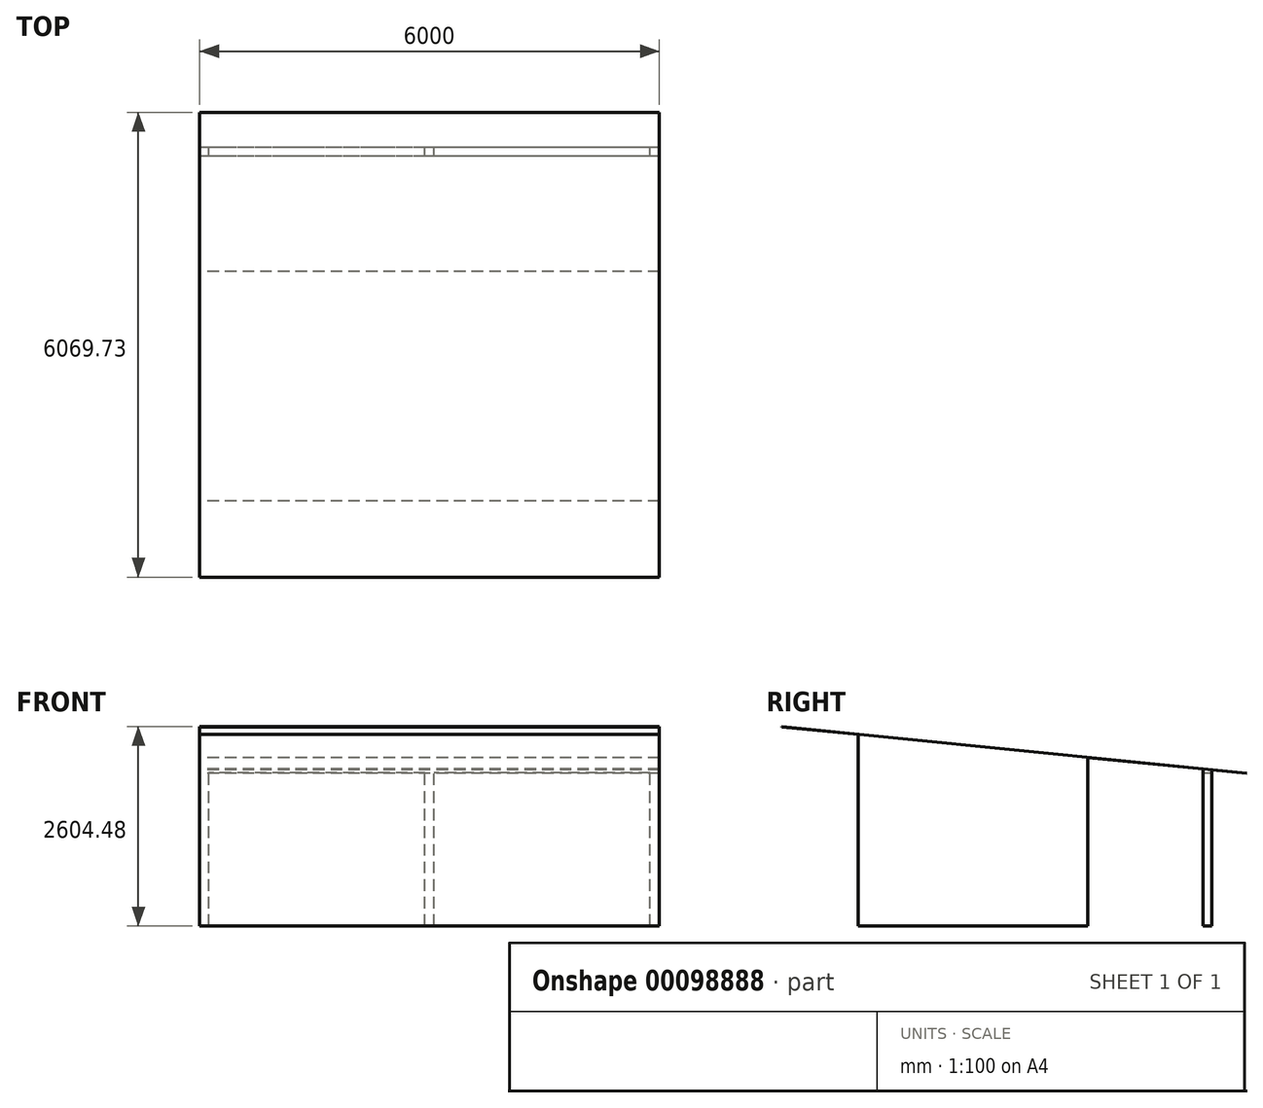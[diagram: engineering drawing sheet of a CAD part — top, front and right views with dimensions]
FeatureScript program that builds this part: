
annotation { "Feature Type Name" : "Feature", "Feature Type Description" : "" }
export const myFeature = defineFeature(function(context is Context, id is Id, definition is map)
    precondition{}
    {
        {
            var Q0;
            Q0=qCreatedBy(makeId("Right.planeOp"),FACE);
            var sketch = newSketch(context, id + "F0", { "sketchPlane" : qUnion([Q0])});
            skLineSegment(sketch, "E0", {"start": v(0, 0) * mm, "end": v(0, 2500) * mm});
            skLineSegment(sketch, "E1", {"start": v(-995.04, 2599.5) * mm, "end": v(5074.69, 1992.53) * mm});
            skLineSegment(sketch, "E2", {"start": v(3000, 2200) * mm, "end": v(3000, 0) * mm});
            skLineSegment(sketch, "E3", {"start": v(3000, 0) * mm, "end": v(0, 0) * mm});
            skLineSegment(sketch, "E4", {"start": v(-995.04, 2599.5) * mm, "end": v(-994.54, 2604.48) * mm});
            skLineSegment(sketch, "E5", {"start": v(-994.54, 2604.48) * mm, "end": v(5074.69, 1997.56) * mm});
            skLineSegment(sketch, "E6", {"start": v(5074.69, 1997.56) * mm, "end": v(5074.69, 1992.53) * mm});
            skLineSegment(sketch, "E7", {"start": v(4500, 0) * mm, "end": v(4500, 2050) * mm});
            skLineSegment(sketch, "E8", {"start": v(4500, 0) * mm, "end": v(4620, 0) * mm});
            skLineSegment(sketch, "E9", {"start": v(4620, 0) * mm, "end": v(4620, 2038) * mm});
            skSolve(sketch);
        }
        {
            var Q0;
            Q0 = qSketchRegion(id + "F0", true);
            extrude(context, id + "F1", {"entities" : qUnion([Q0]), "endBound" : BoundingType.SYMMETRIC, "depth" : 6000 * mm});
        }
        {
            var Q0;
            Q0=makeQuery(id+"F1.opExtrude","SWEPT_FACE",FACE,{"disambiguationData":[OSD([sQuery(id+"F0.wireOp",EDGE,"E9")])]});
            var sketch = newSketch(context, id + "F2", { "sketchPlane" : qUnion([Q0])});
            skLineSegment(sketch, "E10.bottom", {"start": v(-2880, 0) * mm, "end": v(-60, 0) * mm});
            skLineSegment(sketch, "E10.top", {"start": v(-2880, 2000) * mm, "end": v(-60, 2000) * mm});
            skLineSegment(sketch, "E10.left", {"start": v(-2880, 0) * mm, "end": v(-2880, 2000) * mm});
            skLineSegment(sketch, "E10.right", {"start": v(-60, 0) * mm, "end": v(-60, 2000) * mm});
            skLineSegment(sketch, "E11.bottom", {"start": v(60, 0) * mm, "end": v(2880, 0) * mm});
            skLineSegment(sketch, "E11.top", {"start": v(60, 2000) * mm, "end": v(2880, 2000) * mm});
            skLineSegment(sketch, "E11.left", {"start": v(60, 0) * mm, "end": v(60, 2000) * mm});
            skLineSegment(sketch, "E11.right", {"start": v(2880, 0) * mm, "end": v(2880, 2000) * mm});
            skLineSegment(sketch, "E12", {"start": v(0, 0) * mm, "end": v(0, 670.67) * mm, "construction": true});
            skSolve(sketch);
        }
        {
            var Q0;
            Q0 = qSketchRegion(id + "F2", true);
            extrude(context, id + "F3", {"entities" : qUnion([Q0]), "operationType" : NewBodyOperationType.REMOVE, "endBound" : BoundingType.UP_TO_NEXT, "oppositeDirection" : true, "depth" : 25 * mm});
        }
    });
